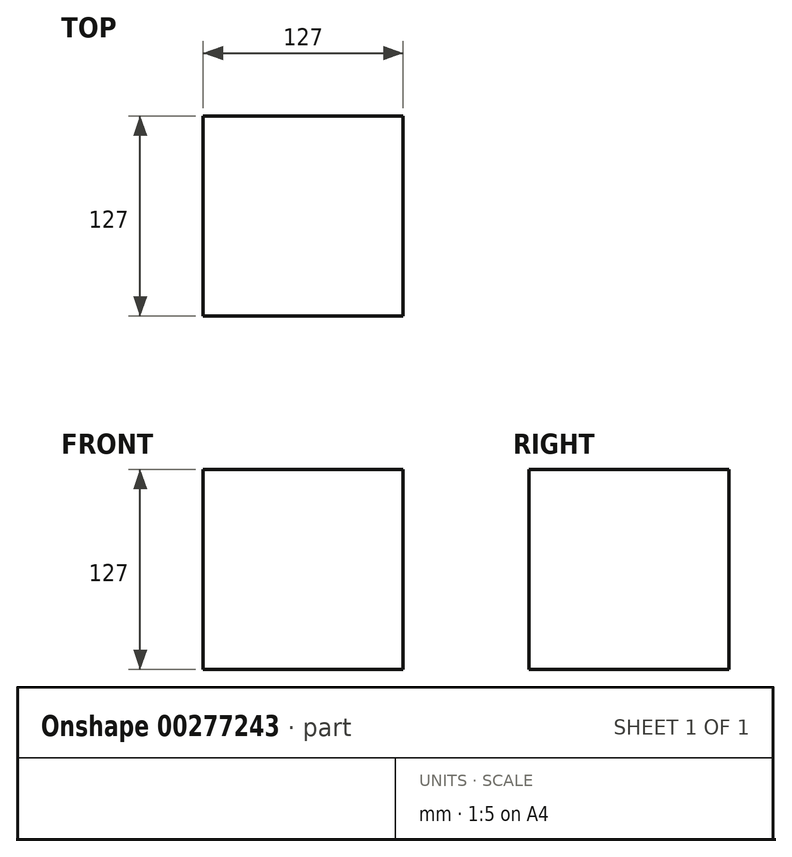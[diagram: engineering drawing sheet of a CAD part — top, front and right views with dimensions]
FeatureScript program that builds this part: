
annotation { "Feature Type Name" : "Feature", "Feature Type Description" : "" }
export const myFeature = defineFeature(function(context is Context, id is Id, definition is map)
    precondition{}
    {
        {
            var Q0;
            Q0=qCreatedBy(makeId("Top.planeOp"),FACE);
            var sketch = newSketch(context, id + "F0", { "sketchPlane" : qUnion([Q0])});
            skLineSegment(sketch, "E0.bottom", {"start": v(67.78, -41.77) * mm, "end": v(-59.22, -41.77) * mm});
            skLineSegment(sketch, "E0.top", {"start": v(67.78, 85.23) * mm, "end": v(-59.22, 85.23) * mm});
            skLineSegment(sketch, "E0.left", {"start": v(67.78, -41.77) * mm, "end": v(67.78, 85.23) * mm});
            skLineSegment(sketch, "E0.right", {"start": v(-59.22, -41.77) * mm, "end": v(-59.22, 85.23) * mm});
            skPoint(sketch, "E0.middle", {"position": v(4.28, 21.73) * mm});
            skSolve(sketch);
        }
        {
            var Q0;
            Q0 = qSketchRegion(id + "F0", true);
            extrude(context, id + "F1", {"entities" : qUnion([Q0]), "endBound" : BoundingType.SYMMETRIC, "depth" : 127 * mm});
        }
    });
